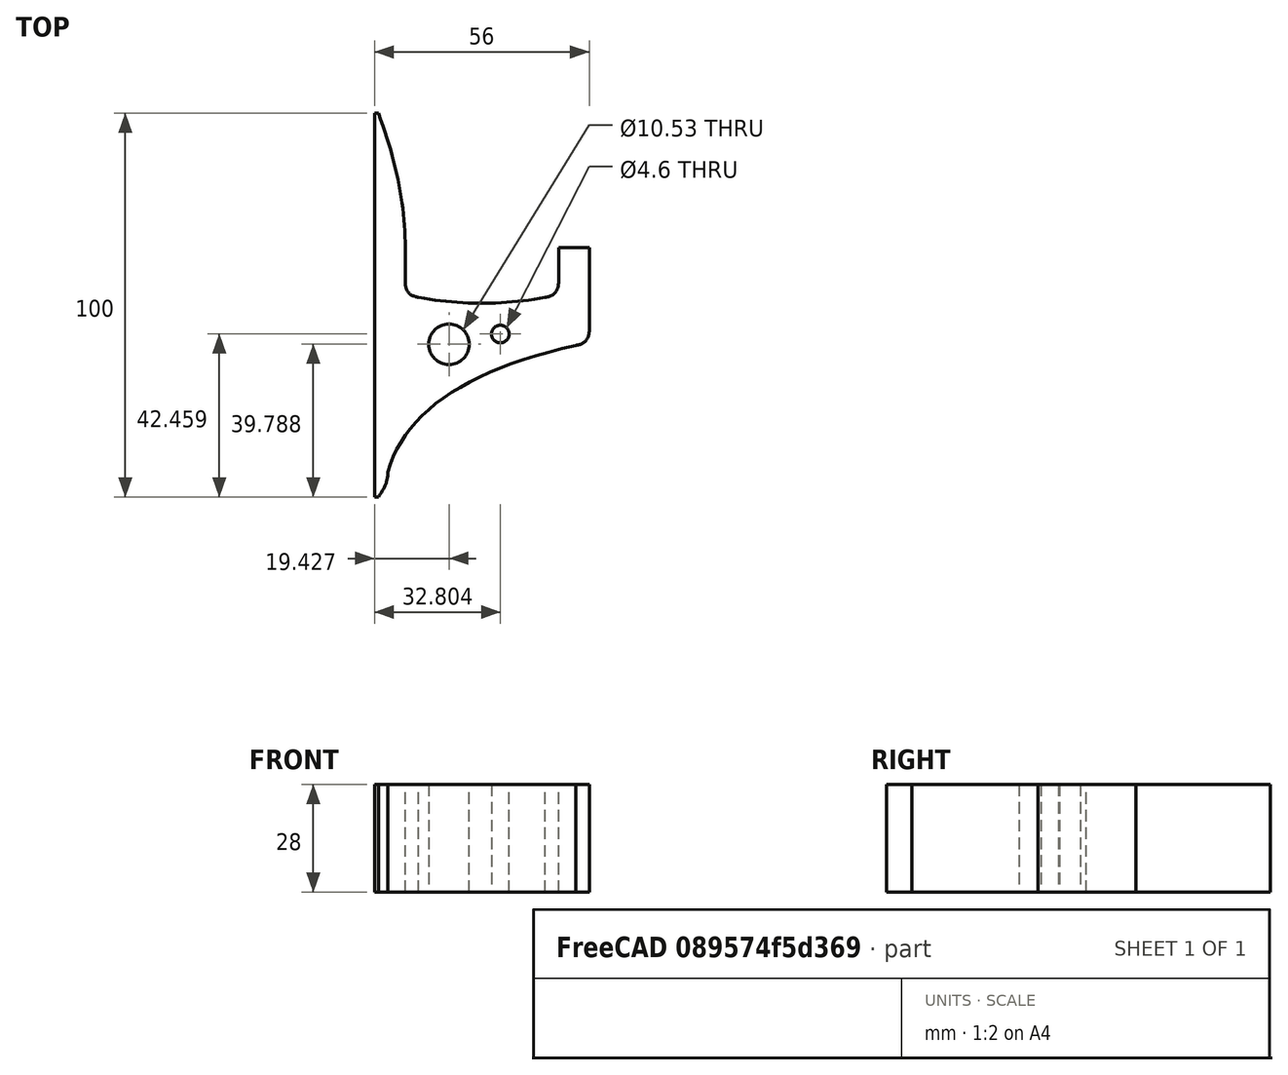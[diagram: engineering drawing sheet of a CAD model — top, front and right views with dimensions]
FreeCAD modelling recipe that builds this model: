
FCSTD DOCUMENT  (FreeCAD 0.19R0.19.2)
Label: headphoneStandWithHookStudsRemovedCurrent_2
License: All rights reserved
LicenseURL: http://en.wikipedia.org/wiki/All_rights_reserved
objects: Sketcher::SketchObject×1, Part::Extrusion×1
note: 2 computed .brp shape members not serialized (recipe doc carries the construction recipe); baked Part::Feature solids carry a one-line shape summary decoded from their .brp

FEATURE [Sketcher::SketchObject] Sketch
  FullyConstrained = false
  sketch-geometry (51):
    g0: LineSegment StartX=0 StartY=0 StartZ=0 EndX=0 EndY=100 EndZ=0
    g1: LineSegment StartX=8 StartY=65 StartZ=0 EndX=8 EndY=56 EndZ=0
    g2: Circle CenterX=8 CenterY=56 CenterZ=0 NormalX=0 NormalY=0 NormalZ=1 AngleXU=0 Radius=1
    g3: Circle CenterX=8 CenterY=52.5 CenterZ=0 NormalX=0 NormalY=0 NormalZ=1 AngleXU=0 Radius=1
    g4: Circle CenterX=11.5 CenterY=52 CenterZ=0 NormalX=0 NormalY=0 NormalZ=1 AngleXU=0 Radius=1
    g5: BSplineCurve PolesCount=3 KnotsCount=2 Degree=2 IsPeriodic=0
    g6: GeomPoint X=8 Y=56 Z=0
    g7: GeomPoint X=11.5 Y=52 Z=0
    g8: Circle CenterX=44.5 CenterY=52 CenterZ=0 NormalX=0 NormalY=0 NormalZ=1 AngleXU=0 Radius=1
    g9: Circle CenterX=48 CenterY=52.5 CenterZ=0 NormalX=0 NormalY=0 NormalZ=1 AngleXU=0 Radius=1
    g10: Circle CenterX=48 CenterY=56 CenterZ=0 NormalX=0 NormalY=0 NormalZ=1 AngleXU=0 Radius=1
    g11: BSplineCurve PolesCount=3 KnotsCount=2 Degree=2 IsPeriodic=0
    g12: GeomPoint X=44.5 Y=52 Z=0
    g13: GeomPoint X=48 Y=56 Z=0
    g14: Circle CenterX=11.5 CenterY=52 CenterZ=0 NormalX=0 NormalY=0 NormalZ=1 AngleXU=0 Radius=1
    g15: Circle CenterX=28 CenterY=49 CenterZ=0 NormalX=0 NormalY=0 NormalZ=1 AngleXU=0 Radius=1
    g16: Circle CenterX=44.5 CenterY=52 CenterZ=0 NormalX=0 NormalY=0 NormalZ=1 AngleXU=0 Radius=1
    g17: BSplineCurve PolesCount=3 KnotsCount=2 Degree=2 IsPeriodic=0
    g18: GeomPoint X=11.5 Y=52 Z=0
    g19: GeomPoint X=44.5 Y=52 Z=0
    g20: LineSegment StartX=48 StartY=65 StartZ=0 EndX=48 EndY=56 EndZ=0
    g21: LineSegment StartX=48 StartY=65 StartZ=0 EndX=56 EndY=65 EndZ=0
    g22: LineSegment StartX=56 StartY=65 StartZ=0 EndX=56 EndY=43.5 EndZ=0
    g23: Circle CenterX=56 CenterY=43.5 CenterZ=0 NormalX=0 NormalY=0 NormalZ=1 AngleXU=0 Radius=1
    g24: Circle CenterX=56 CenterY=40 CenterZ=0 NormalX=0 NormalY=0 NormalZ=1 AngleXU=0 Radius=1
    g25: Circle CenterX=52.5 CenterY=39.5 CenterZ=0 NormalX=0 NormalY=0 NormalZ=1 AngleXU=0 Radius=1
    g26: BSplineCurve PolesCount=3 KnotsCount=2 Degree=2 IsPeriodic=0
    g27: GeomPoint X=56 Y=43.5 Z=0
    g28: GeomPoint X=52.5 Y=39.5 Z=0
    g29: LineSegment StartX=0 StartY=0 StartZ=0 EndX=1 EndY=0 EndZ=0
    g30: LineSegment StartX=0 StartY=100 StartZ=0 EndX=1 EndY=100 EndZ=0
    g31: Circle CenterX=8 CenterY=65 CenterZ=0 NormalX=0 NormalY=0 NormalZ=1 AngleXU=0 Radius=1
    g32: Circle CenterX=8 CenterY=81.5 CenterZ=0 NormalX=0 NormalY=0 NormalZ=1 AngleXU=0 Radius=1
    g33: Circle CenterX=1 CenterY=100 CenterZ=0 NormalX=0 NormalY=0 NormalZ=1 AngleXU=0 Radius=1
    g34: BSplineCurve PolesCount=3 KnotsCount=2 Degree=2 IsPeriodic=0
    g35: GeomPoint X=8 Y=65 Z=0
    g36: GeomPoint X=1 Y=100 Z=0
    g37: Circle CenterX=1 CenterY=0 CenterZ=0 NormalX=0 NormalY=0 NormalZ=1 AngleXU=0 Radius=1
    g38: Circle CenterX=3.5 CenterY=3.3 CenterZ=0 NormalX=0 NormalY=0 NormalZ=1 AngleXU=0 Radius=1
    g39: Circle CenterX=3.5 CenterY=6.5 CenterZ=0 NormalX=0 NormalY=0 NormalZ=1 AngleXU=0 Radius=1
    g40: BSplineCurve PolesCount=3 KnotsCount=2 Degree=2 IsPeriodic=0
    g41: GeomPoint X=1 Y=0 Z=0
    g42: GeomPoint X=3.5 Y=6.5 Z=0
    g43: Circle CenterX=52.5 CenterY=39.5 CenterZ=0 NormalX=0 NormalY=0 NormalZ=1 AngleXU=0 Radius=1
    g44: Circle CenterX=10 CenterY=30 CenterZ=0 NormalX=0 NormalY=0 NormalZ=1 AngleXU=0 Radius=1
    g45: Circle CenterX=3.5 CenterY=6.5 CenterZ=0 NormalX=0 NormalY=0 NormalZ=1 AngleXU=0 Radius=1
    g46: BSplineCurve PolesCount=3 KnotsCount=2 Degree=2 IsPeriodic=0
    g47: GeomPoint X=52.5 Y=39.5 Z=0
    g48: GeomPoint X=3.5 Y=6.5 Z=0
    g49: Circle CenterX=19.4268 CenterY=39.7877 CenterZ=0 NormalX=0 NormalY=0 NormalZ=1 AngleXU=0 Radius=5.26565
    g50: Circle CenterX=32.8037 CenterY=42.4589 CenterZ=0 NormalX=0 NormalY=0 NormalZ=1 AngleXU=0 Radius=2.29927
  constraints (92):
    c: Vertical(g0)
    c: Distance(g0) = 100
    c: Coincident(g0,g-1)
    c: Block(g0)
    c: Vertical(g1)
    c: Distance(g1) = 9
    c: Block(g1)
    c: Weight(g2) = 1
    c: Equal(g2,g3)
    c: Equal(g2,g4)
    c: InternalAlignment(g2,g5)
    c: InternalAlignment(g3,g5)
    c: InternalAlignment(g4,g5)
    c: InternalAlignment(g6,g5)
    c: InternalAlignment(g7,g5)
    c: Coincident(g5,g1)
    c: Block(g5)
    c: Weight(g8) = 1
    c: Equal(g8,g9)
    c: Equal(g8,g10)
    c: InternalAlignment(g8,g11)
    c: InternalAlignment(g9,g11)
    c: InternalAlignment(g10,g11)
    c: InternalAlignment(g12,g11)
    c: InternalAlignment(g13,g11)
    c: Block(g11)
    c: Weight(g14) = 1
    c: Equal(g14,g15)
    c: Equal(g14,g16)
    c: InternalAlignment(g14,g17)
    c: InternalAlignment(g15,g17)
    c: InternalAlignment(g16,g17)
    c: InternalAlignment(g18,g17)
    c: InternalAlignment(g19,g17)
    c: Coincident(g17,g5)
    c: Coincident(g17,g11)
    c: Block(g17)
    c: Vertical(g20)
    c: Coincident(g20,g11)
    c: Equal(g1,g20)
    c: Horizontal(g21)
    c: Coincident(g21,g20)
    c: Distance(g21) = 8
    c: Vertical(g22)
    c: Block(g21)
    c: Coincident(g22,g21)
    c: Distance(g22) = 21.5
    c: Weight(g23) = 1
    c: Equal(g23,g24)
    c: Equal(g23,g25)
    c: InternalAlignment(g23,g26)
    c: InternalAlignment(g24,g26)
    c: InternalAlignment(g25,g26)
    c: InternalAlignment(g27,g26)
    c: InternalAlignment(g28,g26)
    c: Coincident(g26,g22)
    c: Block(g26)
    c: Horizontal(g29)
    c: Distance(g29) = 1
    c: Coincident(g29,g0)
    c: Block(g29)
    c: Horizontal(g30)
    c: Distance(g30) = 1
    c: Coincident(g30,g0)
    c: Block(g30)
    c: Weight(g31) = 1
    c: Equal(g31,g32)
    c: Equal(g31,g33)
    c: InternalAlignment(g31,g34)
    c: InternalAlignment(g32,g34)
    c: InternalAlignment(g33,g34)
    c: InternalAlignment(g35,g34)
    c: InternalAlignment(g36,g34)
    c: Coincident(g34,g30)
    c: Coincident(g34,g1)
    c: Block(g34)
    c: Weight(g37) = 1
    c: Equal(g37,g38)
    c: Equal(g37,g39)
    c: InternalAlignment(g37,g40)
    c: InternalAlignment(g38,g40)
    c: InternalAlignment(g39,g40)
    c: InternalAlignment(g41,g40)
    c: InternalAlignment(g44,g46)
    c: InternalAlignment(g45,g46)
    c: InternalAlignment(g47,g46)
    c: InternalAlignment(g48,g46)
    c: Coincident(g46,g40)
    c: Coincident(g46,g26)
    c: Block(g46)
    c: Block(g49)
    c: Block(g50)
FEATURE [Part::Extrusion] Extrude
  Base = -> Sketch
  Dir = (0,0,1)
  DirMode = 2
  FaceMakerClass = Part::FaceMakerBullseye
  LengthFwd = 28
  LengthRev = 0
  Solid = true
  Symmetric = false
